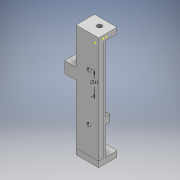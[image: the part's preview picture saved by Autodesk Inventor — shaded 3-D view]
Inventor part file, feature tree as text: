
AUTODESK INVENTOR PART (.ipt)
format: ipt  version: 2018 (Build 220112000, 112)  size: 519,680 bytes
history: native  units: mm
features: sketch x28, extrude x18, hole x6, fillet x3
ambient origin geometry x8: Origin, YZ Plane, XZ Plane, XY Plane, X Axis, Y Axis, Z Axis, Center Point
bodies: Solid1 (feature_tree)
feature tree (55):
  extrude  "Extrusion1"  Depth=100.0mm
  extrude  "Extrusion2"  Depth=5.0mm
  sketch  "Sketch3"  dims[d5=5.0mm d6=40.0mm d7=0.0mm]
  hole  "Hole1"  [1 undecoded]
  extrude  "Extrusion3"  Depth=23.0mm
  hole  "Hole2"  [1 undecoded]
  fillet  "Fillet1"  Radius=8.5mm
  extrude  "Extrusion4"  TaperAngle=90.0deg  [1 undecoded]
  extrude  "Extrusion5"  TaperAngle=180.0deg  [1 undecoded]
  hole  "Hole3"  [1 undecoded]
  fillet  "Fillet2"  Radius=3.5mm
  extrude  "Extrusion6"  Depth=10.0mm
  extrude  "Extrusion7"  Depth=5.0mm TaperAngle=0.0deg
  extrude  "Extrusion8"  Depth=5.0mm TaperAngle=0.0deg
  extrude  "Extrusion9"  Depth=0.1mm
  hole  "Hole4"  [1 undecoded]
  extrude  "Extrusion10"  Depth=5.5mm
  hole  "Hole5"  [1 undecoded]
  extrude  "Extrusion11"  Depth=2.1mm TaperAngle=0.0deg
  extrude  "Extrusion12"  Depth=5.0mm
  extrude  "Extrusion13"  Depth=1.0mm TaperAngle=0.0deg
  extrude  "Extrusion14"  Depth=3.8mm TaperAngle=0.0deg
  sketch  "Sketch21"  dims[d66=6.35mm d67=3.8mm d68=0.0mm]
  extrude  "Extrusion15"  Depth=4.55mm TaperAngle=0.0deg
  sketch  "Sketch23"  dims[d78=3.3mm d79=6.0mm d80=4.0mm d81=2.0mm d82=90.0deg d83=80.0mm d84=20.594885mm d85=5.45mm]
  extrude  "Extrusion16"  Depth=5.45mm
  extrude  "Extrusion17"  Depth=10.5mm
  hole  "Hole6"  [1 undecoded]
  fillet  "Fillet3"  Radius=4.5mm
  extrude  "Extrusion18"  Depth=15.5mm TaperAngle=0.0deg
  sketch  "Sketch28"  dims[d99=10.0mm d100=4.1mm d101=0.0mm d102=5.0mm d103=17.5mm d104=10.0mm d105=0.0mm d106=5.0mm d107=6.0mm d108=6.0mm d109=4.0mm d110=2.0mm d111=90.0deg d112=80.0mm d113=20.594885mm d114=1.0mm d115=45.0mm d116=0.0mm d117=21.0mm]
  sketch  "Sketch1"  dims[d0=22.65mm d1=100.0mm]
  sketch  "Sketch2"  dims[d2=5.0mm d3=0.0mm d4=5.0mm]
  sketch  "Sketch4"  dims[d8=10.0mm]
  sketch  "Sketch5"  dims[d9=4.0mm d10=6.0mm d11=4.0mm d12=2.0mm d13=90.0deg d14=115.0mm d15=20.594885mm d16=23.0mm]
  sketch  "Sketch6"  dims[d17=102.75mm d18=0.0mm d19=1.175mm d20=8.5mm]
  sketch  "Sketch7"  dims[d21=21.0mm d22=90.0deg]
  sketch  "Sketch8"  dims[d23=8.5mm d24=180.0deg]
  sketch  "Sketch9"  dims[d25=21.0mm]
  sketch  "Sketch10"  dims[d26=4.0mm d27=6.0mm d28=4.0mm d29=2.0mm d30=90.0deg d31=115.0mm d32=20.594885mm d33=1.0mm d34=3.5mm]
  sketch  "Sketch11"  dims[d35=15.825mm d36=10.0mm]
  sketch  "Sketch12"  dims[d37=10.0mm d38=5.0mm d39=0.0mm]
  sketch  "Sketch13"  dims[d40=5.0mm d41=12.5mm d42=0.0mm]
  sketch  "Sketch14"  dims[d43=6.0mm d44=6.0mm d45=4.0mm d46=2.0mm d47=90.0deg d48=115.0mm d49=20.594885mm d50=0.1mm]
  sketch  "Sketch15"  dims[d51=4.25mm d52=1000.0mm d53=0.0mm]
  sketch  "Sketch16"  dims[d54=3.3mm d55=5.5mm]
  sketch  "Sketch17"  dims[d56=3.2mm d57=3.0mm]
  sketch  "Sketch18"  dims[d58=2.1mm d59=91.25mm d60=0.0mm]
  sketch  "Sketch19"  dims[d61=4.44mm d62=5.0mm]
  sketch  "Sketch20"  dims[d63=1.0mm d64=91.25mm d65=0.0mm]
  sketch  "Sketch22"  dims[d69=3.3mm d70=6.0mm d71=4.0mm d72=2.0mm d73=90.0deg d74=8.0mm d75=20.594885mm d76=4.55mm d77=0.0mm]
  sketch  "Sketch24"  dims[d86=129.8mm d87=0.0mm d88=10.5mm]
  sketch  "Sketch25"  dims[d89=2.5mm d90=0.0mm d91=10.0mm d92=4.5mm d93=0.0mm]
  sketch  "Sketch26"  dims[d94=8.0mm d95=0.0mm d96=15.5mm d97=0.0mm]
  sketch  "Sketch27"  dims[d98=10.0mm]
note: 8 required parameter values undecoded (feature->parameter linkage not recoverable at this tier; creation-order binding heuristic only, values carry confidence <= 0.55)
